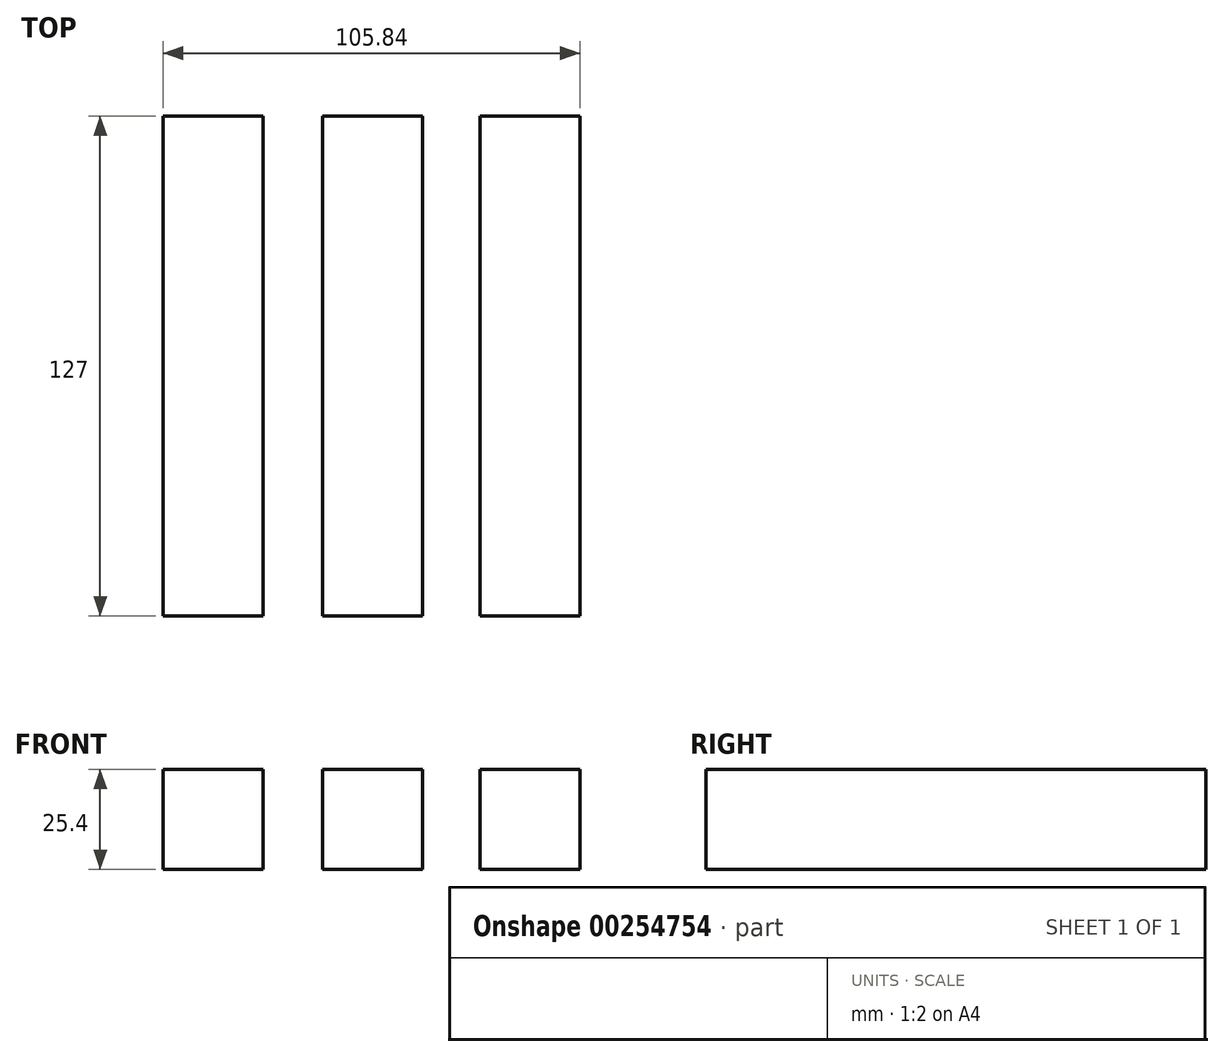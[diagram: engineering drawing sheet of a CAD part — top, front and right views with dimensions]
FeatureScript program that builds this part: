
annotation { "Feature Type Name" : "Feature", "Feature Type Description" : "" }
export const myFeature = defineFeature(function(context is Context, id is Id, definition is map)
    precondition{}
    {
        {
            var Q0;
            Q0=qCreatedBy(makeId("Front.planeOp"),FACE);
            var sketch = newSketch(context, id + "F0", { "sketchPlane" : qUnion([Q0])});
            skLineSegment(sketch, "E0.bottom", {"start": v(12.7, -12.7) * mm, "end": v(-12.7, -12.7) * mm});
            skLineSegment(sketch, "E0.top", {"start": v(12.7, 12.7) * mm, "end": v(-12.7, 12.7) * mm});
            skLineSegment(sketch, "E0.left", {"start": v(12.7, -12.7) * mm, "end": v(12.7, 12.7) * mm});
            skLineSegment(sketch, "E0.right", {"start": v(-12.7, -12.7) * mm, "end": v(-12.7, 12.7) * mm});
            skPoint(sketch, "E0.middle", {"position": v(0, 0) * mm});
            skLineSegment(sketch, "E1.bottom", {"start": v(52.7, -12.7) * mm, "end": v(27.3, -12.7) * mm});
            skLineSegment(sketch, "E1.top", {"start": v(52.7, 12.7) * mm, "end": v(27.3, 12.7) * mm});
            skLineSegment(sketch, "E1.left", {"start": v(52.7, -12.7) * mm, "end": v(52.7, 12.7) * mm});
            skLineSegment(sketch, "E1.right", {"start": v(27.3, -12.7) * mm, "end": v(27.3, 12.7) * mm});
            skPoint(sketch, "E1.middle", {"position": v(40, 0) * mm});
            skLineSegment(sketch, "E2.bottom", {"start": v(-27.74, -12.7) * mm, "end": v(-53.14, -12.7) * mm});
            skLineSegment(sketch, "E2.top", {"start": v(-27.74, 12.7) * mm, "end": v(-53.14, 12.7) * mm});
            skLineSegment(sketch, "E2.left", {"start": v(-27.74, -12.7) * mm, "end": v(-27.74, 12.7) * mm});
            skLineSegment(sketch, "E2.right", {"start": v(-53.14, -12.7) * mm, "end": v(-53.14, 12.7) * mm});
            skPoint(sketch, "E2.middle", {"position": v(-40.44, 0) * mm});
            skSolve(sketch);
        }
        {
            var Q0;
            Q0=makeQuery(id+"F0.imprint","IMPRINT",FACE,{"disambiguationData":[TD([[makeQuery(id+"F0.imprint","IMPRINT",EDGE,{"derivedFrom":sQuery(id+"F0.wireOp",EDGE,"E2.bottom")}),-1.0]])]});
            extrude(context, id + "F1", {"entities" : qUnion([Q0]), "endBound" : BoundingType.SYMMETRIC, "depth" : 127 * mm});
        }
        {
            var Q0;
            Q0=makeQuery(id+"F0.imprint","IMPRINT",FACE,{"disambiguationData":[TD([[makeQuery(id+"F0.imprint","IMPRINT",EDGE,{"derivedFrom":sQuery(id+"F0.wireOp",EDGE,"E0.bottom")}),-1.0]])]});
            extrude(context, id + "F2", {"entities" : qUnion([Q0]), "endBound" : BoundingType.SYMMETRIC, "depth" : 127 * mm});
        }
        {
            var Q0;
            Q0=makeQuery(id+"F0.imprint","IMPRINT",FACE,{"disambiguationData":[TD([[makeQuery(id+"F0.imprint","IMPRINT",EDGE,{"derivedFrom":sQuery(id+"F0.wireOp",EDGE,"E1.bottom")}),-1.0]])]});
            extrude(context, id + "F3", {"entities" : qUnion([Q0]), "endBound" : BoundingType.SYMMETRIC, "depth" : 127 * mm});
        }
    });
